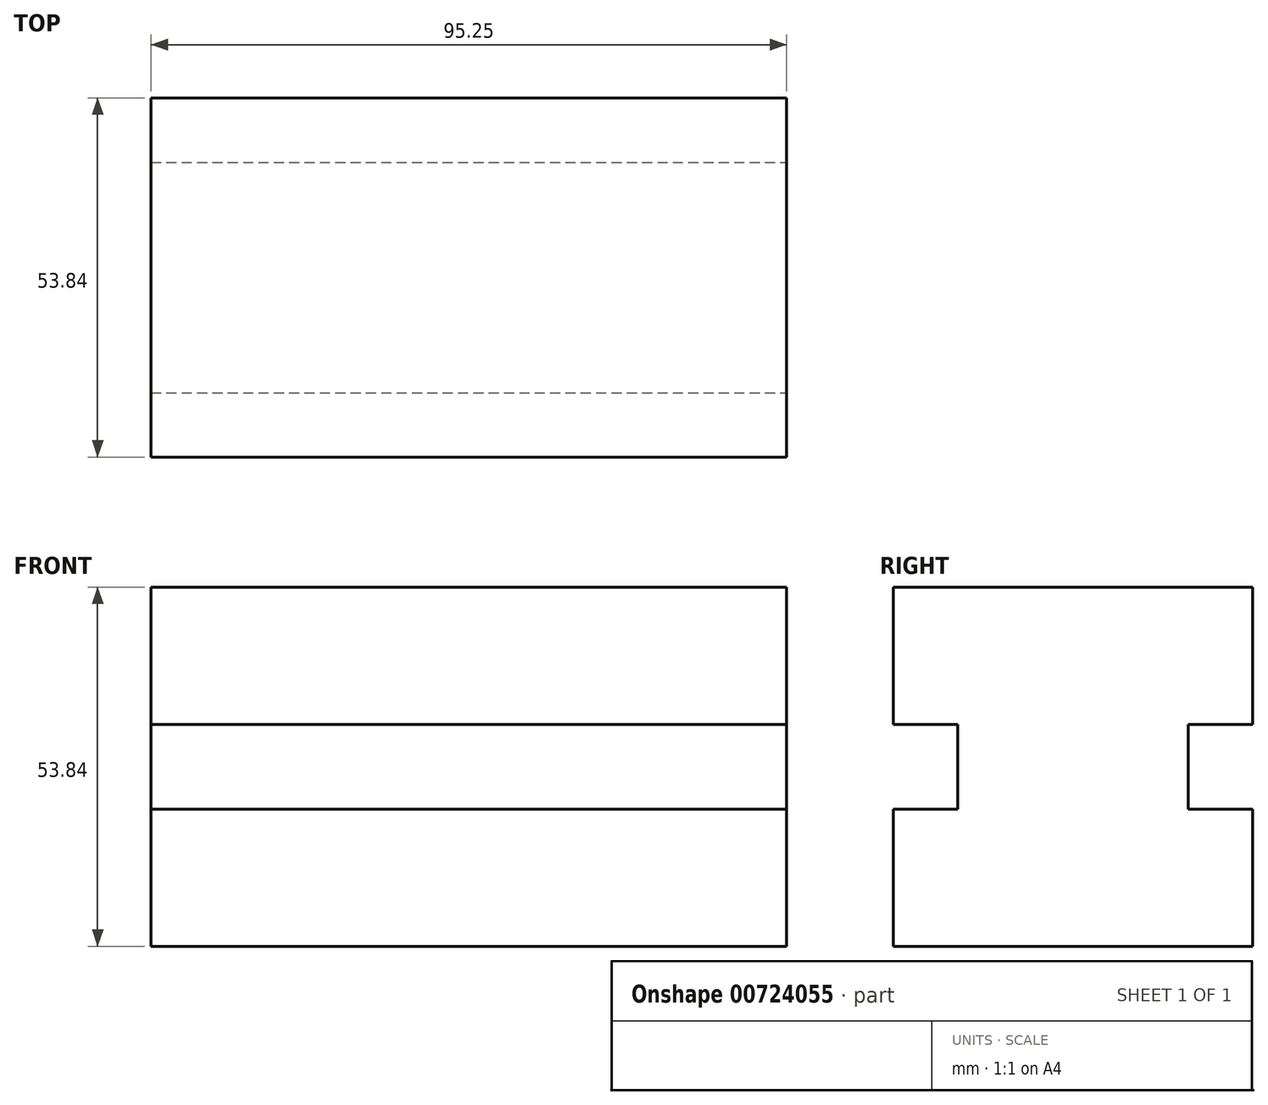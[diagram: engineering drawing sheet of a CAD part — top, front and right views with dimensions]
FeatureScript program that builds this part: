
annotation { "Feature Type Name" : "Feature", "Feature Type Description" : "" }
export const myFeature = defineFeature(function(context is Context, id is Id, definition is map)
    precondition{}
    {
        {
            var Q0;
            Q0=qCreatedBy(makeId("Right.planeOp"),FACE);
            var sketch = newSketch(context, id + "F0", { "sketchPlane" : qUnion([Q0])});
            skLineSegment(sketch, "E0.bottom", {"start": v(26.92, -26.92) * mm, "end": v(-26.92, -26.92) * mm});
            skLineSegment(sketch, "E0.top", {"start": v(26.92, 26.92) * mm, "end": v(-26.92, 26.92) * mm});
            skLineSegment(sketch, "E0.left", {"start": v(26.92, -26.92) * mm, "end": v(26.92, -6.35) * mm});
            skLineSegment(sketch, "E0.right", {"start": v(-26.92, -26.92) * mm, "end": v(-26.92, -6.35) * mm});
            skPoint(sketch, "E0.middle", {"position": v(0, 0) * mm});
            skLineSegment(sketch, "E1.bottom", {"start": v(-26.92, 6.35) * mm, "end": v(-17.27, 6.35) * mm});
            skLineSegment(sketch, "E1.left", {"start": v(-26.92, -6.35) * mm, "end": v(-26.92, -12.7) * mm});
            skLineSegment(sketch, "E2", {"start": v(-17.27, 6.35) * mm, "end": v(-17.27, -6.35) * mm});
            skLineSegment(sketch, "E3", {"start": v(-17.27, -6.35) * mm, "end": v(-26.92, -6.35) * mm});
            skLineSegment(sketch, "E4.trimOffspring", {"start": v(-26.92, 6.35) * mm, "end": v(-26.92, 26.92) * mm});
            skLineSegment(sketch, "E5", {"start": v(0, 35.38) * mm, "end": v(0, -26.92) * mm, "construction": true});
            skLineSegment(sketch, "E6.MirrorCS", {"start": v(26.92, 6.35) * mm, "end": v(17.27, 6.35) * mm});
            skLineSegment(sketch, "E7.MirrorCS", {"start": v(17.27, 6.35) * mm, "end": v(17.27, -6.35) * mm});
            skLineSegment(sketch, "E8.MirrorCS", {"start": v(17.27, -6.35) * mm, "end": v(26.92, -6.35) * mm});
            skLineSegment(sketch, "E9.trimOffspring", {"start": v(26.92, 6.35) * mm, "end": v(26.92, 26.92) * mm});
            skSolve(sketch);
        }
        {
            var Q0;
            Q0=makeQuery(id+"F0.imprint","IMPRINT",FACE,{"disambiguationData":[TD([[makeQuery(id+"F0.imprint","IMPRINT",EDGE,{"derivedFrom":sQuery(id+"F0.wireOp",EDGE,"E0.bottom")}),-1.0]])]});
            extrude(context, id + "F1", {"entities" : qUnion([Q0]), "oppositeDirection" : true, "depth" : 95.25 * mm, "offsetDistance" : 25.4 * mm});
        }
    });
